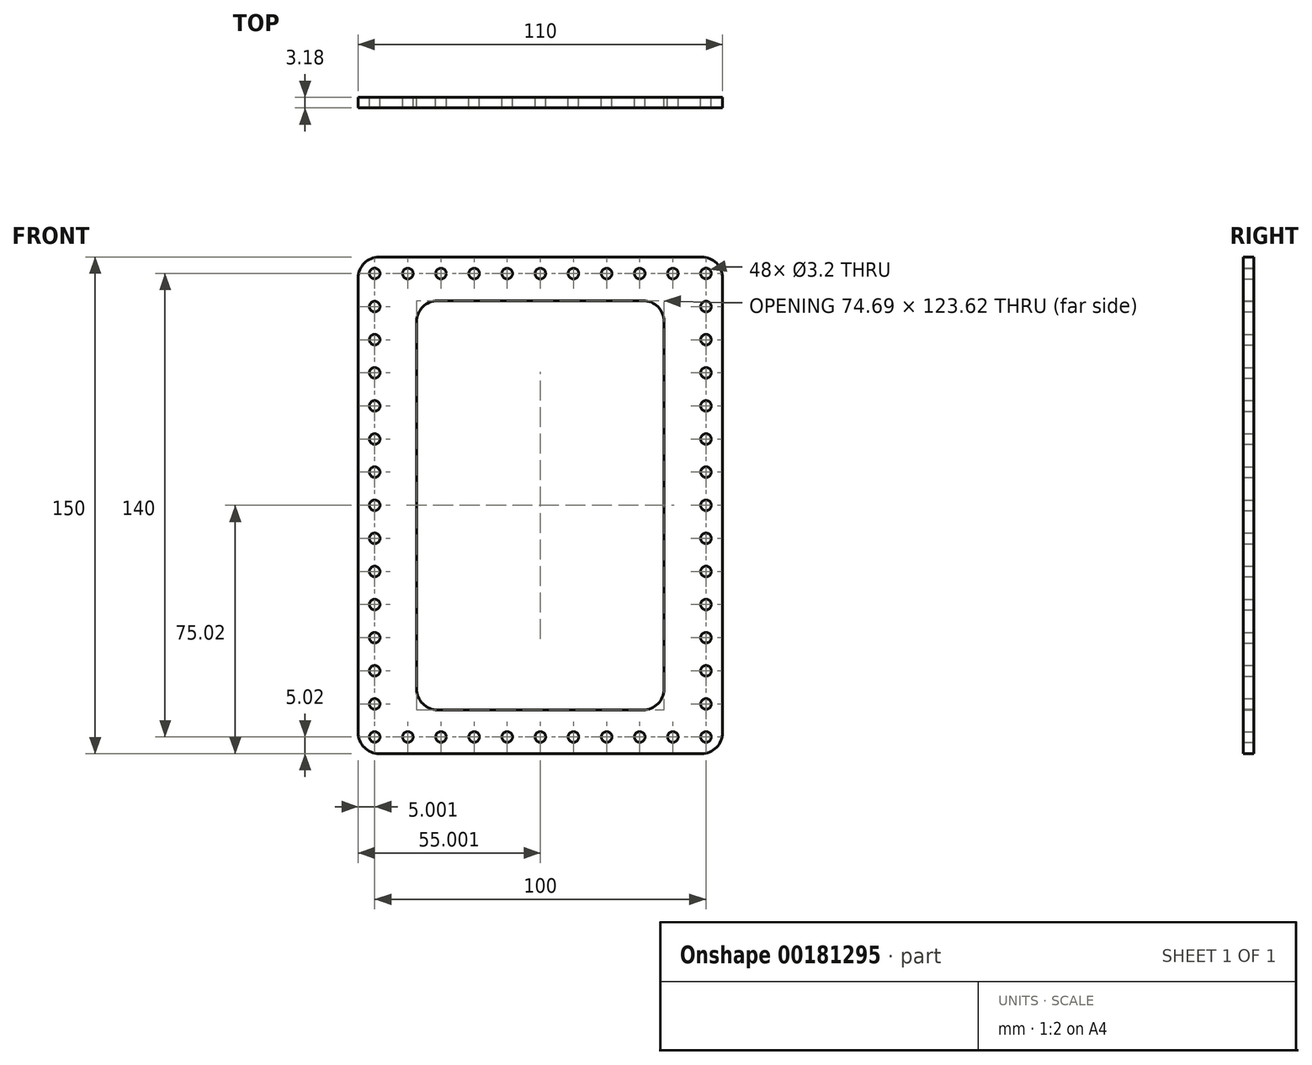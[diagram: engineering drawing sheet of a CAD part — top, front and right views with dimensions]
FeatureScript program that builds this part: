
annotation { "Feature Type Name" : "Feature", "Feature Type Description" : "" }
export const myFeature = defineFeature(function(context is Context, id is Id, definition is map)
    precondition{}
    {
        {
            var Q0;
            Q0=qCreatedBy(makeId("Front.planeOp"),FACE);
            var sketch = newSketch(context, id + "F0", { "sketchPlane" : qUnion([Q0])});
            skLineSegment(sketch, "E0.bottom", {"start": v(-16.56, 62.25) * mm, "end": v(45.43, 62.25) * mm});
            skLineSegment(sketch, "E0.top", {"start": v(-16.56, -61.37) * mm, "end": v(45.43, -61.37) * mm});
            skLineSegment(sketch, "E0.left", {"start": v(-22.91, 55.9) * mm, "end": v(-22.91, -55.02) * mm});
            skLineSegment(sketch, "E0.right", {"start": v(51.78, 55.9) * mm, "end": v(51.78, -55.02) * mm});
            skArc(sketch, "E1.filletArc", {"start": v(-16.56, 62.25) * mm, "mid": v(-21.05, 60.4) * mm, "end": v(-22.91, 55.9) * mm});
            skArc(sketch, "E2.filletArc", {"start": v(51.78, 55.9) * mm, "mid": v(49.92, 60.4) * mm, "end": v(45.43, 62.25) * mm});
            skArc(sketch, "E3.filletArc", {"start": v(45.43, -61.37) * mm, "mid": v(49.92, -59.51) * mm, "end": v(51.78, -55.02) * mm});
            skArc(sketch, "E4.filletArc", {"start": v(-22.91, -55.02) * mm, "mid": v(-21.05, -59.51) * mm, "end": v(-16.56, -61.37) * mm});
            skLineSegment(sketch, "E5.bottom", {"start": v(-34.22, 75.42) * mm, "end": v(63.08, 75.42) * mm});
            skLineSegment(sketch, "E5.top", {"start": v(-34.22, -74.58) * mm, "end": v(63.08, -74.58) * mm});
            skLineSegment(sketch, "E5.left", {"start": v(-40.57, 69.07) * mm, "end": v(-40.57, -68.23) * mm});
            skLineSegment(sketch, "E5.right", {"start": v(69.43, 69.07) * mm, "end": v(69.43, -68.23) * mm});
            skPoint(sketch, "E6.visualSharp", {"position": v(-40.57, 75.42) * mm});
            skArc(sketch, "E6.filletArc", {"start": v(-34.22, 75.42) * mm, "mid": v(-38.7, 73.56) * mm, "end": v(-40.57, 69.07) * mm});
            skPoint(sketch, "E7.visualSharp", {"position": v(69.43, 75.42) * mm});
            skArc(sketch, "E7.filletArc", {"start": v(69.43, 69.07) * mm, "mid": v(67.57, 73.56) * mm, "end": v(63.08, 75.42) * mm});
            skPoint(sketch, "E8.visualSharp", {"position": v(69.43, -74.58) * mm});
            skArc(sketch, "E8.filletArc", {"start": v(63.08, -74.58) * mm, "mid": v(67.57, -72.72) * mm, "end": v(69.43, -68.23) * mm});
            skPoint(sketch, "E9.visualSharp", {"position": v(-40.57, -74.58) * mm});
            skArc(sketch, "E9.filletArc", {"start": v(-40.57, -68.23) * mm, "mid": v(-38.7, -72.72) * mm, "end": v(-34.22, -74.58) * mm});
            skCircle(sketch, "E10", {"center": v(-35.57, 0.44) * mm, "radius": 1.6 * mm});
            skCircle(sketch, "E11.0.1.0", {"center": v(-35.57, 10.44) * mm, "radius": 1.6 * mm});
            skCircle(sketch, "E11.0.2.0", {"center": v(-35.57, 20.44) * mm, "radius": 1.6 * mm});
            skCircle(sketch, "E11.0.3.0", {"center": v(-35.57, 30.44) * mm, "radius": 1.6 * mm});
            skCircle(sketch, "E11.0.4.0", {"center": v(-35.57, 40.44) * mm, "radius": 1.6 * mm});
            skCircle(sketch, "E11.0.5.0", {"center": v(-35.57, 50.44) * mm, "radius": 1.6 * mm});
            skCircle(sketch, "E11.0.6.0", {"center": v(-35.57, 60.44) * mm, "radius": 1.6 * mm});
            skCircle(sketch, "E11.0.7.0", {"center": v(-35.57, 70.44) * mm, "radius": 1.6 * mm});
            skLineSegment(sketch, "E11.direction1", {"start": v(-35.57, 0.44) * mm, "end": v(-10.17, 0.44) * mm, "construction": true});
            skLineSegment(sketch, "E11.direction2", {"start": v(-35.57, 0.44) * mm, "end": v(-35.57, 10.44) * mm, "construction": true});
            skCircle(sketch, "E12.MirrorC", {"center": v(-35.57, -9.56) * mm, "radius": 1.6 * mm});
            skCircle(sketch, "E13.MirrorC", {"center": v(-35.57, -19.56) * mm, "radius": 1.6 * mm});
            skCircle(sketch, "E14.MirrorC", {"center": v(-35.57, -29.56) * mm, "radius": 1.6 * mm});
            skCircle(sketch, "E15.MirrorC", {"center": v(-35.57, -39.56) * mm, "radius": 1.6 * mm});
            skCircle(sketch, "E16.MirrorC", {"center": v(-35.57, -49.56) * mm, "radius": 1.6 * mm});
            skCircle(sketch, "E17.MirrorC", {"center": v(-35.57, -59.56) * mm, "radius": 1.6 * mm});
            skCircle(sketch, "E18.MirrorC", {"center": v(-35.57, -69.56) * mm, "radius": 1.6 * mm});
            skPoint(sketch, "E19.endSnap0", {"position": v(14.43, 62.25) * mm});
            skCircle(sketch, "E20.MirrorC", {"center": v(64.43, 70.44) * mm, "radius": 1.6 * mm});
            skCircle(sketch, "E21.MirrorC", {"center": v(64.43, 60.44) * mm, "radius": 1.6 * mm});
            skCircle(sketch, "E22.MirrorC", {"center": v(64.43, 50.44) * mm, "radius": 1.6 * mm});
            skCircle(sketch, "E23.MirrorC", {"center": v(64.43, 40.44) * mm, "radius": 1.6 * mm});
            skCircle(sketch, "E24.MirrorC", {"center": v(64.43, 30.44) * mm, "radius": 1.6 * mm});
            skCircle(sketch, "E25.MirrorC", {"center": v(64.43, 20.44) * mm, "radius": 1.6 * mm});
            skCircle(sketch, "E26.MirrorC", {"center": v(64.43, 10.44) * mm, "radius": 1.6 * mm});
            skCircle(sketch, "E27.MirrorC", {"center": v(64.43, -9.56) * mm, "radius": 1.6 * mm});
            skCircle(sketch, "E28.MirrorC", {"center": v(64.43, 0.44) * mm, "radius": 1.6 * mm});
            skCircle(sketch, "E29.MirrorC", {"center": v(64.43, -19.56) * mm, "radius": 1.6 * mm});
            skCircle(sketch, "E30.MirrorC", {"center": v(64.43, -29.56) * mm, "radius": 1.6 * mm});
            skCircle(sketch, "E31.MirrorC", {"center": v(64.43, -39.56) * mm, "radius": 1.6 * mm});
            skCircle(sketch, "E32.MirrorC", {"center": v(64.43, -49.56) * mm, "radius": 1.6 * mm});
            skCircle(sketch, "E33.MirrorC", {"center": v(64.43, -59.56) * mm, "radius": 1.6 * mm});
            skCircle(sketch, "E34.MirrorC", {"center": v(64.43, -69.56) * mm, "radius": 1.6 * mm});
            skCircle(sketch, "E35", {"center": v(14.43, 70.42) * mm, "radius": 1.6 * mm});
            skCircle(sketch, "E36.1.0.0", {"center": v(24.43, 70.42) * mm, "radius": 1.6 * mm});
            skCircle(sketch, "E36.2.0.0", {"center": v(34.43, 70.42) * mm, "radius": 1.6 * mm});
            skCircle(sketch, "E36.3.0.0", {"center": v(44.43, 70.42) * mm, "radius": 1.6 * mm});
            skCircle(sketch, "E36.4.0.0", {"center": v(54.43, 70.42) * mm, "radius": 1.6 * mm});
            skLineSegment(sketch, "E36.direction1", {"start": v(14.43, 70.42) * mm, "end": v(24.43, 70.42) * mm, "construction": true});
            skCircle(sketch, "E37.MirrorC", {"center": v(4.43, 70.42) * mm, "radius": 1.6 * mm});
            skCircle(sketch, "E38.MirrorC", {"center": v(-5.57, 70.42) * mm, "radius": 1.6 * mm});
            skCircle(sketch, "E39.MirrorC", {"center": v(-15.57, 70.42) * mm, "radius": 1.6 * mm});
            skCircle(sketch, "E40.MirrorC", {"center": v(-25.57, 70.42) * mm, "radius": 1.6 * mm});
            skCircle(sketch, "E41.MirrorC", {"center": v(-25.57, -69.54) * mm, "radius": 1.6 * mm});
            skCircle(sketch, "E42.MirrorC", {"center": v(-15.57, -69.54) * mm, "radius": 1.6 * mm});
            skCircle(sketch, "E43.MirrorC", {"center": v(-5.57, -69.54) * mm, "radius": 1.6 * mm});
            skCircle(sketch, "E44.MirrorC", {"center": v(4.43, -69.54) * mm, "radius": 1.6 * mm});
            skCircle(sketch, "E45.MirrorC", {"center": v(24.43, -69.54) * mm, "radius": 1.6 * mm});
            skCircle(sketch, "E46.MirrorC", {"center": v(34.43, -69.54) * mm, "radius": 1.6 * mm});
            skCircle(sketch, "E47.MirrorC", {"center": v(44.43, -69.54) * mm, "radius": 1.6 * mm});
            skCircle(sketch, "E48.MirrorC", {"center": v(54.43, -69.54) * mm, "radius": 1.6 * mm});
            skCircle(sketch, "E49.MirrorC", {"center": v(14.43, -69.54) * mm, "radius": 1.6 * mm});
            skSolve(sketch);
        }
        {
            var Q0;
            Q0=makeQuery(id+"F0.imprint","IMPRINT",FACE,{"disambiguationData":[TD([[makeQuery(id+"F0.imprint","IMPRINT",EDGE,{"derivedFrom":sQuery(id+"F0.wireOp",EDGE,"E0.bottom")}),1.0]])]});
            extrude(context, id + "F1", {"entities" : qUnion([Q0]), "depth" : 3.17 * mm});
        }
    });
